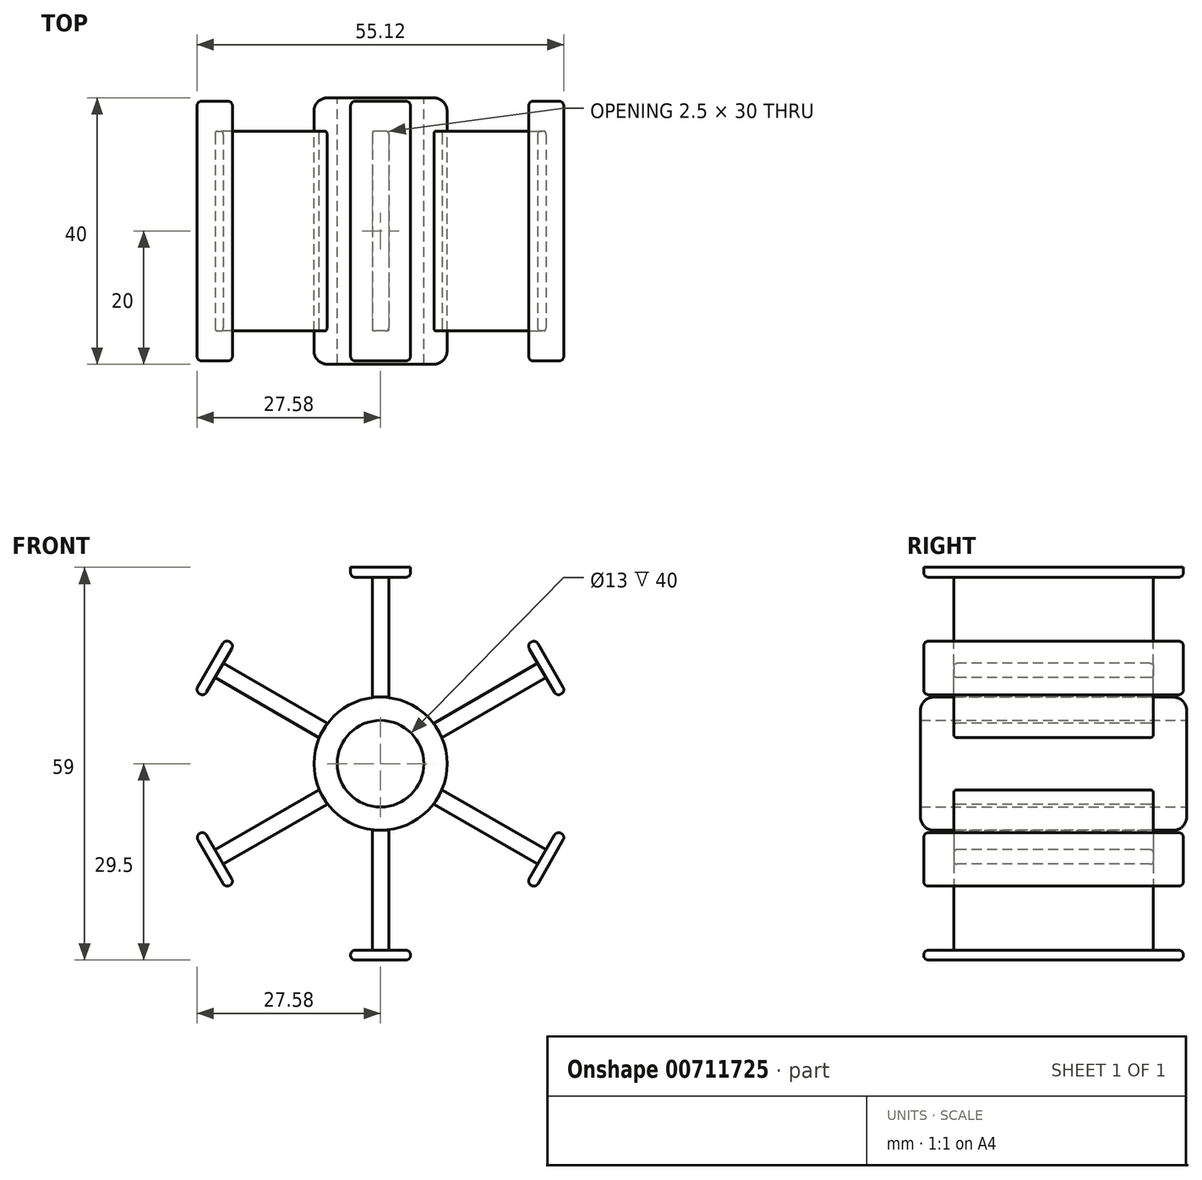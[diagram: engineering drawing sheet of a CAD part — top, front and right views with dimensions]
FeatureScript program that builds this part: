
annotation { "Feature Type Name" : "Feature", "Feature Type Description" : "" }
export const myFeature = defineFeature(function(context is Context, id is Id, definition is map)
    precondition{}
    {
        {
            var Q0;
            Q0=qCreatedBy(makeId("Front.planeOp"),FACE);
            var sketch = newSketch(context, id + "F0", { "sketchPlane" : qUnion([Q0])});
            skCircle(sketch, "E0", {"center": v(0, 0) * mm, "radius": 31 * mm});
            skCircle(sketch, "E1", {"center": v(0, 0) * mm, "radius": 6 * mm});
            skCircle(sketch, "E2", {"center": v(0, 0) * mm, "radius": 6.5 * mm});
            skCircle(sketch, "E3", {"center": v(0, 0) * mm, "radius": 10 * mm});
            skLineSegment(sketch, "E4", {"start": v(0, 10) * mm, "end": v(0, 28) * mm});
            skLineSegment(sketch, "E5.1.0", {"start": v(-8.66, -5) * mm, "end": v(-24.25, -14) * mm});
            skLineSegment(sketch, "E5.2.0", {"start": v(8.66, -5) * mm, "end": v(24.25, -14) * mm});
            skLineSegment(sketch, "E6", {"start": v(0, -10) * mm, "end": v(0, -28) * mm});
            skLineSegment(sketch, "E7.1.0", {"start": v(-8.66, 5) * mm, "end": v(-24.25, 14) * mm});
            skLineSegment(sketch, "E7.2.0", {"start": v(8.66, 5) * mm, "end": v(24.25, 14) * mm});
            skSolve(sketch);
        }
        {
            var Q0;
            Q0=makeQuery(id+"F0.imprint","IMPRINT",FACE,{"disambiguationData":[TD([[makeQuery(id+"F0.imprint","IMPRINT",EDGE,{"derivedFrom":sQuery(id+"F0.wireOp",EDGE,"E2")}),-1.0]])]});
            extrude(context, id + "F1", {"entities" : qUnion([Q0]), "endBound" : BoundingType.SYMMETRIC, "depth" : 40 * mm, "offsetDistance" : 25 * mm});
        }
        {
            var Q0;
            Q0=sQuery(id+"F0.wireOp",EDGE,"E4");
            var Q1;
            Q1=sQuery(id+"F0.wireOp",EDGE,"E5.2.0");
            var Q2;
            Q2=sQuery(id+"F0.wireOp",EDGE,"E5.1.0");
            var Q3;
            Q3=sQuery(id+"F0.wireOp",EDGE,"E7.1.0");
            var Q4;
            Q4=sQuery(id+"F0.wireOp",EDGE,"E7.2.0");
            var Q5;
            Q5=sQuery(id+"F0.wireOp",EDGE,"E6");
            extrude(context, id + "F2", {"bodyType" : ToolBodyType.SURFACE, "surfaceEntities" : qUnion([Q0, Q1, Q2, Q3, Q4, Q5]), "endBound" : BoundingType.SYMMETRIC, "depth" : 30 * mm, "offsetDistance" : 25 * mm});
        }
        {
            var Q0;
            Q0=makeQuery(id+"F2.opExtrude","SWEPT_FACE",FACE,{"disambiguationData":[OSD([sQuery(id+"F0.wireOp",EDGE,"E4")])]});
            extrude(context, id + "F3", {"entities" : qUnion([Q0]), "operationType" : NewBodyOperationType.ADD, "endBound" : BoundingType.SYMMETRIC, "depth" : 2.5 * mm, "offsetDistance" : 25 * mm});
        }
        {
            var Q0;
            Q0=makeQuery(id+"F2.opExtrude","SWEPT_FACE",FACE,{"disambiguationData":[OSD([sQuery(id+"F0.wireOp",EDGE,"E5.1.0")])]});
            extrude(context, id + "F4", {"entities" : qUnion([Q0]), "operationType" : NewBodyOperationType.ADD, "endBound" : BoundingType.SYMMETRIC, "depth" : 2.5 * mm, "offsetDistance" : 25 * mm});
        }
        {
            var Q0;
            Q0=makeQuery(id+"F2.opExtrude","SWEPT_FACE",FACE,{"disambiguationData":[OSD([sQuery(id+"F0.wireOp",EDGE,"E5.2.0")])]});
            extrude(context, id + "F5", {"entities" : qUnion([Q0]), "operationType" : NewBodyOperationType.ADD, "endBound" : BoundingType.SYMMETRIC, "depth" : 2.5 * mm, "offsetDistance" : 25 * mm});
        }
        {
            var Q0;
            {var subQ0=sQuery(id+"F0.wireOp",EDGE,"E5.1.0");Q0=makeQuery(id+"F4.opExtrude","CAP_EDGE",EDGE,{"disambiguationData":[OSD([subQ0]),TDD([makeQuery(id+"F2.opExtrude","CAP_EDGE",EDGE,{"disambiguationData":[OSD([subQ0])],"isStart":false})])],"isStart":false});}
            var Q1;
            {var subQ0=sQuery(id+"F0.wireOp",EDGE,"E5.1.0");Q1=makeQuery(id+"F4.opExtrude","CAP_EDGE",EDGE,{"disambiguationData":[OSD([subQ0]),TDD([makeQuery(id+"F2.opExtrude","CAP_EDGE",EDGE,{"disambiguationData":[OSD([subQ0])],"isStart":false})])],"isStart":true});}
            var Q2;
            {var subQ0=sQuery(id+"F0.wireOp",EDGE,"E5.1.0");Q2=makeQuery(id+"F4.opExtrude","CAP_EDGE",EDGE,{"disambiguationData":[OSD([subQ0]),TDD([makeQuery(id+"F2.opExtrude","CAP_EDGE",EDGE,{"disambiguationData":[OSD([subQ0])],"isStart":true})])],"isStart":true});}
            var Q3;
            {var subQ0=sQuery(id+"F0.wireOp",EDGE,"E5.1.0");Q3=makeQuery(id+"F4.opExtrude","CAP_EDGE",EDGE,{"disambiguationData":[OSD([subQ0]),TDD([makeQuery(id+"F2.opExtrude","CAP_EDGE",EDGE,{"disambiguationData":[OSD([subQ0])],"isStart":true})])],"isStart":false});}
            var Q4;
            {var subQ0=sQuery(id+"F0.wireOp",EDGE,"E4");Q4=makeQuery(id+"F3.opExtrude","CAP_EDGE",EDGE,{"disambiguationData":[OSD([subQ0]),TDD([makeQuery(id+"F2.opExtrude","CAP_EDGE",EDGE,{"disambiguationData":[OSD([subQ0])],"isStart":false})])],"isStart":true});}
            var Q5;
            {var subQ0=sQuery(id+"F0.wireOp",EDGE,"E4");Q5=makeQuery(id+"F3.opExtrude","CAP_EDGE",EDGE,{"disambiguationData":[OSD([subQ0]),TDD([makeQuery(id+"F2.opExtrude","CAP_EDGE",EDGE,{"disambiguationData":[OSD([subQ0])],"isStart":false})])],"isStart":false});}
            var Q6;
            {var subQ0=sQuery(id+"F0.wireOp",EDGE,"E4");Q6=makeQuery(id+"F3.opExtrude","CAP_EDGE",EDGE,{"disambiguationData":[OSD([subQ0]),TDD([makeQuery(id+"F2.opExtrude","CAP_EDGE",EDGE,{"disambiguationData":[OSD([subQ0])],"isStart":true})])],"isStart":false});}
            var Q7;
            {var subQ0=sQuery(id+"F0.wireOp",EDGE,"E4");Q7=makeQuery(id+"F3.opExtrude","CAP_EDGE",EDGE,{"disambiguationData":[OSD([subQ0]),TDD([makeQuery(id+"F2.opExtrude","CAP_EDGE",EDGE,{"disambiguationData":[OSD([subQ0])],"isStart":true})])],"isStart":true});}
            var Q8;
            {var subQ0=sQuery(id+"F0.wireOp",EDGE,"E5.2.0");Q8=makeQuery(id+"F5.opExtrude","CAP_EDGE",EDGE,{"disambiguationData":[OSD([subQ0]),TDD([makeQuery(id+"F2.opExtrude","CAP_EDGE",EDGE,{"disambiguationData":[OSD([subQ0])],"isStart":true})])],"isStart":true});}
            var Q9;
            {var subQ0=sQuery(id+"F0.wireOp",EDGE,"E5.2.0");Q9=makeQuery(id+"F5.opExtrude","CAP_EDGE",EDGE,{"disambiguationData":[OSD([subQ0]),TDD([makeQuery(id+"F2.opExtrude","CAP_EDGE",EDGE,{"disambiguationData":[OSD([subQ0])],"isStart":true})])],"isStart":false});}
            var Q10;
            {var subQ0=sQuery(id+"F0.wireOp",EDGE,"E5.2.0");Q10=makeQuery(id+"F5.opExtrude","CAP_EDGE",EDGE,{"disambiguationData":[OSD([subQ0]),TDD([makeQuery(id+"F2.opExtrude","CAP_EDGE",EDGE,{"disambiguationData":[OSD([subQ0])],"isStart":false})])],"isStart":true});}
            var Q11;
            {var subQ0=sQuery(id+"F0.wireOp",EDGE,"E5.2.0");Q11=makeQuery(id+"F5.opExtrude","CAP_EDGE",EDGE,{"disambiguationData":[OSD([subQ0]),TDD([makeQuery(id+"F2.opExtrude","CAP_EDGE",EDGE,{"disambiguationData":[OSD([subQ0])],"isStart":false})])],"isStart":false});}
            fillet(context, id + "F6", {"entities" : qUnion([Q0, Q1, Q2, Q3, Q4, Q5, Q6, Q7, Q8, Q9, Q10, Q11]), "radius" : 0.5 * mm, "tangentPropagation" : true, "allowEdgeOverflow" : false});
        }
        {
            var Q0;
            Q0=makeQuery(id+"F5.opExtrude","SWEPT_FACE",FACE,{"disambiguationData":[OSD([sQuery(id+"F0.wireOp",VERTEX,"E5.2.0.end")])]});
            var sketch = newSketch(context, id + "F7", { "sketchPlane" : qUnion([Q0])});
            skLineSegment(sketch, "E8.bottom", {"start": v(19.5, 4.5) * mm, "end": v(-19.5, 4.5) * mm});
            skLineSegment(sketch, "E8.top", {"start": v(19.5, -4.5) * mm, "end": v(-19.5, -4.5) * mm});
            skLineSegment(sketch, "E8.left", {"start": v(19.5, 4.5) * mm, "end": v(19.5, -4.5) * mm});
            skLineSegment(sketch, "E8.right", {"start": v(-19.5, 4.5) * mm, "end": v(-19.5, -4.5) * mm});
            skPoint(sketch, "E8.middle", {"position": v(0, 0) * mm});
            skSolve(sketch);
        }
        {
            var Q0;
            Q0 = qSketchRegion(id + "F7", true);
            extrude(context, id + "F8", {"entities" : qUnion([Q0]), "operationType" : NewBodyOperationType.ADD, "depth" : 1.5 * mm, "offsetDistance" : 25 * mm});
        }
        {
            var Q0;
            Q0=makeQuery(id+"F5.opExtrude","CAP_EDGE",EDGE,{"disambiguationData":[OSD([sQuery(id+"F0.wireOp",VERTEX,"E5.2.0.end")])],"isStart":true});
            var Q1;
            Q1=makeQuery(id+"F5.opExtrude","CAP_EDGE",EDGE,{"disambiguationData":[OSD([sQuery(id+"F0.wireOp",VERTEX,"E5.2.0.end")])],"isStart":false});
            var Q2;
            Q2=makeQuery(id+"F8.opExtrude","SWEPT_EDGE",EDGE,{"disambiguationData":[OSD([sQuery(id+"F7.wireOp",EDGE,"E8.top"),sQuery(id+"F7.wireOp",EDGE,"E8.right")])]});
            var Q3;
            Q3=makeQuery(id+"F8.opExtrude","SWEPT_EDGE",EDGE,{"disambiguationData":[OSD([sQuery(id+"F7.wireOp",EDGE,"E8.bottom"),sQuery(id+"F7.wireOp",EDGE,"E8.right")])]});
            var Q4;
            Q4=makeQuery(id+"F8.opExtrude","SWEPT_EDGE",EDGE,{"disambiguationData":[OSD([sQuery(id+"F7.wireOp",EDGE,"E8.top"),sQuery(id+"F7.wireOp",EDGE,"E8.left")])]});
            var Q5;
            Q5=makeQuery(id+"F8.opExtrude","SWEPT_EDGE",EDGE,{"disambiguationData":[OSD([sQuery(id+"F7.wireOp",EDGE,"E8.bottom"),sQuery(id+"F7.wireOp",EDGE,"E8.left")])]});
            var Q6;
            Q6=makeQuery(id+"F8.opExtrude","CAP_EDGE",EDGE,{"disambiguationData":[OSD([sQuery(id+"F7.wireOp",EDGE,"E8.right")])],"isStart":true});
            var Q7;
            Q7=makeQuery(id+"F8.opExtrude","CAP_EDGE",EDGE,{"disambiguationData":[OSD([sQuery(id+"F7.wireOp",EDGE,"E8.bottom")])],"isStart":true});
            var Q8;
            Q8=makeQuery(id+"F8.opExtrude","CAP_EDGE",EDGE,{"disambiguationData":[OSD([sQuery(id+"F7.wireOp",EDGE,"E8.left")])],"isStart":true});
            var Q9;
            Q9=makeQuery(id+"F8.opExtrude","CAP_EDGE",EDGE,{"disambiguationData":[OSD([sQuery(id+"F7.wireOp",EDGE,"E8.top")])],"isStart":true});
            var Q10;
            Q10=makeQuery(id+"F8.opExtrude","CAP_FACE",FACE,{"disambiguationData":[OSD([sQuery(id+"F7.wireOp",EDGE,"E8.bottom"),sQuery(id+"F7.wireOp",EDGE,"E8.top"),sQuery(id+"F7.wireOp",EDGE,"E8.left"),sQuery(id+"F7.wireOp",EDGE,"E8.right")])],"isStart":false});
            fillet(context, id + "F9", {"entities" : qUnion([Q0, Q1, Q2, Q3, Q4, Q5, Q6, Q7, Q8, Q9, Q10]), "radius" : .7 * mm, "tangentPropagation" : true, "allowEdgeOverflow" : false});
        }
        {
            var Q0;
            Q0=makeQuery(id+"F3.opExtrude","SWEPT_FACE",FACE,{"disambiguationData":[OSD([sQuery(id+"F0.wireOp",VERTEX,"E4.end")])]});
            var sketch = newSketch(context, id + "F10", { "sketchPlane" : qUnion([Q0])});
            skLineSegment(sketch, "E9.bottom", {"start": v(4.5, 19.5) * mm, "end": v(-4.5, 19.5) * mm});
            skLineSegment(sketch, "E9.top", {"start": v(4.5, -19.5) * mm, "end": v(-4.5, -19.5) * mm});
            skLineSegment(sketch, "E9.left", {"start": v(4.5, 19.5) * mm, "end": v(4.5, -19.5) * mm});
            skLineSegment(sketch, "E9.right", {"start": v(-4.5, 19.5) * mm, "end": v(-4.5, -19.5) * mm});
            skPoint(sketch, "E9.middle", {"position": v(0, 0) * mm});
            skSolve(sketch);
        }
        {
            var Q0;
            Q0=makeQuery(id+"F10.imprint","IMPRINT",FACE,{"disambiguationData":[TD([[makeQuery(id+"F10.imprint","IMPRINT",EDGE,{"derivedFrom":sQuery(id+"F10.wireOp",EDGE,"E9.bottom")}),1.0]])]});
            var Q1;
            {var subQ0=sQuery(id+"F0.wireOp",VERTEX,"E4.end");Q1=makeQuery(id+"F10.imprint","IMPRINT",FACE,{"disambiguationData":[TD([[makeQuery(id+"F10.imprint","IMPRINT",EDGE,{"derivedFrom":makeQuery(id+"F3.opExtrude","CAP_EDGE",EDGE,{"disambiguationData":[OSD([subQ0])],"isStart":true})}),1.0]])]});}
            extrude(context, id + "F11", {"entities" : qUnion([Q0, Q1]), "operationType" : NewBodyOperationType.ADD, "depth" : 1.5 * mm, "offsetDistance" : 25 * mm});
        }
        {
            var Q0;
            Q0=makeQuery(id+"F11.opExtrude","CAP_EDGE",EDGE,{"disambiguationData":[OSD([sQuery(id+"F10.wireOp",EDGE,"E9.left")])],"isStart":true});
            var Q1;
            Q1=makeQuery(id+"F11.opExtrude","CAP_EDGE",EDGE,{"disambiguationData":[OSD([sQuery(id+"F10.wireOp",EDGE,"E9.right")])],"isStart":true});
            var Q2;
            Q2=makeQuery(id+"F11.opExtrude","SWEPT_EDGE",EDGE,{"disambiguationData":[OSD([sQuery(id+"F10.wireOp",EDGE,"E9.bottom"),sQuery(id+"F10.wireOp",EDGE,"E9.right")])]});
            var Q3;
            Q3=makeQuery(id+"F11.opExtrude","SWEPT_EDGE",EDGE,{"disambiguationData":[OSD([sQuery(id+"F10.wireOp",EDGE,"E9.top"),sQuery(id+"F10.wireOp",EDGE,"E9.right")])]});
            var Q4;
            Q4=makeQuery(id+"F11.opExtrude","SWEPT_EDGE",EDGE,{"disambiguationData":[OSD([sQuery(id+"F10.wireOp",EDGE,"E9.top"),sQuery(id+"F10.wireOp",EDGE,"E9.left")])]});
            var Q5;
            Q5=makeQuery(id+"F11.opExtrude","SWEPT_EDGE",EDGE,{"disambiguationData":[OSD([sQuery(id+"F10.wireOp",EDGE,"E9.bottom"),sQuery(id+"F10.wireOp",EDGE,"E9.left")])]});
            var Q6;
            Q6=makeQuery(id+"F11.opExtrude","CAP_EDGE",EDGE,{"disambiguationData":[OSD([sQuery(id+"F10.wireOp",EDGE,"E9.top")])],"isStart":true});
            var Q7;
            Q7=makeQuery(id+"F11.opExtrude","CAP_EDGE",EDGE,{"disambiguationData":[OSD([sQuery(id+"F10.wireOp",EDGE,"E9.bottom")])],"isStart":true});
            var Q8;
            Q8=makeQuery(id+"F3.opExtrude","CAP_EDGE",EDGE,{"disambiguationData":[OSD([sQuery(id+"F0.wireOp",VERTEX,"E4.end")])],"isStart":false});
            var Q9;
            {var subQ0=sQuery(id+"F0.wireOp",VERTEX,"E4.end");Q9=makeQuery(id+"F3.opExtrude","SWEPT_EDGE",EDGE,{"disambiguationData":[OSD([subQ0]),TDD([makeQuery(id+"F2.opExtrude","CAP_VERTEX",VERTEX,{"disambiguationData":[OSD([subQ0])],"isStart":false})])]});}
            var Q10;
            Q10=makeQuery(id+"F3.opExtrude","CAP_EDGE",EDGE,{"disambiguationData":[OSD([sQuery(id+"F0.wireOp",VERTEX,"E4.end")])],"isStart":true});
            var Q11;
            {var subQ0=sQuery(id+"F0.wireOp",VERTEX,"E4.end");Q11=makeQuery(id+"F3.opExtrude","SWEPT_EDGE",EDGE,{"disambiguationData":[OSD([subQ0]),TDD([makeQuery(id+"F2.opExtrude","CAP_VERTEX",VERTEX,{"disambiguationData":[OSD([subQ0])],"isStart":true})])]});}
            fillet(context, id + "F12", {"entities" : qUnion([Q0, Q1, Q2, Q3, Q4, Q5, Q6, Q7, Q8, Q9, Q10, Q11]), "radius" : .7 * mm, "tangentPropagation" : true, "allowEdgeOverflow" : false});
        }
        {
            var Q0;
            Q0=makeQuery(id+"F4.opExtrude","SWEPT_FACE",FACE,{"disambiguationData":[OSD([sQuery(id+"F0.wireOp",VERTEX,"E5.1.0.end")])]});
            var sketch = newSketch(context, id + "F13", { "sketchPlane" : qUnion([Q0])});
            skLineSegment(sketch, "E10.bottom", {"start": v(-19.5, 4.5) * mm, "end": v(19.5, 4.5) * mm});
            skLineSegment(sketch, "E10.top", {"start": v(-19.5, -4.5) * mm, "end": v(19.5, -4.5) * mm});
            skLineSegment(sketch, "E10.left", {"start": v(-19.5, 4.5) * mm, "end": v(-19.5, -4.5) * mm});
            skLineSegment(sketch, "E10.right", {"start": v(19.5, 4.5) * mm, "end": v(19.5, -4.5) * mm});
            skPoint(sketch, "E10.middle", {"position": v(0, 0) * mm});
            skSolve(sketch);
        }
        {
            var Q0;
            {var subQ0=sQuery(id+"F0.wireOp",VERTEX,"E5.1.0.end");Q0=makeQuery(id+"F13.imprint","IMPRINT",FACE,{"disambiguationData":[TD([[makeQuery(id+"F13.imprint","IMPRINT",EDGE,{"derivedFrom":makeQuery(id+"F4.opExtrude","CAP_EDGE",EDGE,{"disambiguationData":[OSD([subQ0])],"isStart":true})}),1.0]])]});}
            var Q1;
            Q1=makeQuery(id+"F13.imprint","IMPRINT",FACE,{"disambiguationData":[TD([[makeQuery(id+"F13.imprint","IMPRINT",EDGE,{"derivedFrom":sQuery(id+"F13.wireOp",EDGE,"E10.bottom")}),-1.0]])]});
            extrude(context, id + "F14", {"entities" : qUnion([Q0, Q1]), "operationType" : NewBodyOperationType.ADD, "depth" : 1.5 * mm, "offsetDistance" : 25 * mm});
        }
        {
            var Q0;
            Q0=makeQuery(id+"F14.opExtrude","SWEPT_EDGE",EDGE,{"disambiguationData":[OSD([sQuery(id+"F13.wireOp",EDGE,"E10.top"),sQuery(id+"F13.wireOp",EDGE,"E10.left")])]});
            var Q1;
            Q1=makeQuery(id+"F14.opExtrude","SWEPT_EDGE",EDGE,{"disambiguationData":[OSD([sQuery(id+"F13.wireOp",EDGE,"E10.bottom"),sQuery(id+"F13.wireOp",EDGE,"E10.left")])]});
            var Q2;
            Q2=makeQuery(id+"F14.opExtrude","SWEPT_EDGE",EDGE,{"disambiguationData":[OSD([sQuery(id+"F13.wireOp",EDGE,"E10.bottom"),sQuery(id+"F13.wireOp",EDGE,"E10.right")])]});
            var Q3;
            Q3=makeQuery(id+"F14.opExtrude","SWEPT_EDGE",EDGE,{"disambiguationData":[OSD([sQuery(id+"F13.wireOp",EDGE,"E10.top"),sQuery(id+"F13.wireOp",EDGE,"E10.right")])]});
            var Q4;
            Q4=makeQuery(id+"F14.opExtrude","CAP_EDGE",EDGE,{"disambiguationData":[OSD([sQuery(id+"F13.wireOp",EDGE,"E10.bottom")])],"isStart":true});
            var Q5;
            Q5=makeQuery(id+"F14.opExtrude","CAP_EDGE",EDGE,{"disambiguationData":[OSD([sQuery(id+"F13.wireOp",EDGE,"E10.right")])],"isStart":true});
            var Q6;
            Q6=makeQuery(id+"F14.opExtrude","CAP_EDGE",EDGE,{"disambiguationData":[OSD([sQuery(id+"F13.wireOp",EDGE,"E10.top")])],"isStart":true});
            var Q7;
            Q7=makeQuery(id+"F14.opExtrude","CAP_EDGE",EDGE,{"disambiguationData":[OSD([sQuery(id+"F13.wireOp",EDGE,"E10.left")])],"isStart":true});
            var Q8;
            Q8=makeQuery(id+"F4.opExtrude","CAP_EDGE",EDGE,{"disambiguationData":[OSD([sQuery(id+"F0.wireOp",VERTEX,"E5.1.0.end")])],"isStart":true});
            var Q9;
            Q9=makeQuery(id+"F4.opExtrude","CAP_EDGE",EDGE,{"disambiguationData":[OSD([sQuery(id+"F0.wireOp",VERTEX,"E5.1.0.end")])],"isStart":false});
            var Q10;
            {var subQ0=sQuery(id+"F0.wireOp",VERTEX,"E5.1.0.end");Q10=makeQuery(id+"F4.opExtrude","SWEPT_EDGE",EDGE,{"disambiguationData":[OSD([subQ0]),TDD([makeQuery(id+"F2.opExtrude","CAP_VERTEX",VERTEX,{"disambiguationData":[OSD([subQ0])],"isStart":true})])]});}
            var Q11;
            {var subQ0=sQuery(id+"F0.wireOp",VERTEX,"E5.1.0.end");Q11=makeQuery(id+"F4.opExtrude","SWEPT_EDGE",EDGE,{"disambiguationData":[OSD([subQ0]),TDD([makeQuery(id+"F2.opExtrude","CAP_VERTEX",VERTEX,{"disambiguationData":[OSD([subQ0])],"isStart":false})])]});}
            var Q12;
            Q12=makeQuery(id+"F14.opExtrude","CAP_FACE",FACE,{"disambiguationData":[OSD([sQuery(id+"F13.wireOp",EDGE,"E10.bottom"),sQuery(id+"F13.wireOp",EDGE,"E10.top"),sQuery(id+"F13.wireOp",EDGE,"E10.left"),sQuery(id+"F13.wireOp",EDGE,"E10.right")])],"isStart":false});
            fillet(context, id + "F15", {"entities" : qUnion([Q0, Q1, Q2, Q3, Q4, Q5, Q6, Q7, Q8, Q9, Q10, Q11, Q12]), "radius" : .7 * mm, "tangentPropagation" : true, "allowEdgeOverflow" : false});
        }
        {
            var Q0;
            Q0=makeQuery(id+"F1.opExtrude","CAP_EDGE",EDGE,{"disambiguationData":[OSD([sQuery(id+"F0.wireOp",EDGE,"E3")])],"isStart":true});
            var Q1;
            Q1=makeQuery(id+"F1.opExtrude","CAP_EDGE",EDGE,{"disambiguationData":[OSD([sQuery(id+"F0.wireOp",EDGE,"E3")])],"isStart":false});
            fillet(context, id + "F16", {"entities" : qUnion([Q0, Q1]), "radius" : 2 * mm, "tangentPropagation" : true, "allowEdgeOverflow" : false});
        }
        {
            var Q0;
            Q0=makeQuery(id+"F2.opExtrude","SWEPT_FACE",FACE,{"disambiguationData":[OSD([sQuery(id+"F0.wireOp",EDGE,"E7.2.0")])]});
            extrude(context, id + "F17", {"entities" : qUnion([Q0]), "operationType" : NewBodyOperationType.ADD, "endBound" : BoundingType.SYMMETRIC, "depth" : 2.5 * mm, "offsetDistance" : 25 * mm});
        }
        {
            var Q0;
            Q0=makeQuery(id+"F2.opExtrude","SWEPT_FACE",FACE,{"disambiguationData":[OSD([sQuery(id+"F0.wireOp",EDGE,"E7.1.0")])]});
            extrude(context, id + "F18", {"entities" : qUnion([Q0]), "operationType" : NewBodyOperationType.ADD, "endBound" : BoundingType.SYMMETRIC, "depth" : 2.5 * mm, "offsetDistance" : 25 * mm});
        }
        {
            var Q0;
            Q0=makeQuery(id+"F2.opExtrude","SWEPT_FACE",FACE,{"disambiguationData":[OSD([sQuery(id+"F0.wireOp",EDGE,"E6")])]});
            extrude(context, id + "F19", {"entities" : qUnion([Q0]), "operationType" : NewBodyOperationType.ADD, "endBound" : BoundingType.SYMMETRIC, "depth" : 2.5 * mm, "offsetDistance" : 25 * mm});
        }
        {
            var Q0;
            Q0=makeQuery(id+"F19.opExtrude","SWEPT_FACE",FACE,{"disambiguationData":[OSD([sQuery(id+"F0.wireOp",VERTEX,"E6.end")])]});
            var sketch = newSketch(context, id + "F20", { "sketchPlane" : qUnion([Q0])});
            skLineSegment(sketch, "E11.bottom", {"start": v(4.5, 19.5) * mm, "end": v(-4.5, 19.5) * mm});
            skLineSegment(sketch, "E11.top", {"start": v(4.5, -19.5) * mm, "end": v(-4.5, -19.5) * mm});
            skLineSegment(sketch, "E11.left", {"start": v(4.5, 19.5) * mm, "end": v(4.5, -19.5) * mm});
            skLineSegment(sketch, "E11.right", {"start": v(-4.5, 19.5) * mm, "end": v(-4.5, -19.5) * mm});
            skPoint(sketch, "E11.middle", {"position": v(0, 0) * mm});
            skSolve(sketch);
        }
        {
            var Q0;
            Q0=makeQuery(id+"F17.opExtrude","SWEPT_FACE",FACE,{"disambiguationData":[OSD([sQuery(id+"F0.wireOp",VERTEX,"E7.2.0.end")])]});
            var sketch = newSketch(context, id + "F21", { "sketchPlane" : qUnion([Q0])});
            skLineSegment(sketch, "E12.bottom", {"start": v(19.5, 4.5) * mm, "end": v(-19.5, 4.5) * mm});
            skLineSegment(sketch, "E12.top", {"start": v(19.5, -4.5) * mm, "end": v(-19.5, -4.5) * mm});
            skLineSegment(sketch, "E12.left", {"start": v(19.5, 4.5) * mm, "end": v(19.5, -4.5) * mm});
            skLineSegment(sketch, "E12.right", {"start": v(-19.5, 4.5) * mm, "end": v(-19.5, -4.5) * mm});
            skPoint(sketch, "E12.middle", {"position": v(0, 0) * mm});
            skSolve(sketch);
        }
        {
            var Q0;
            Q0=makeQuery(id+"F18.opExtrude","SWEPT_FACE",FACE,{"disambiguationData":[OSD([sQuery(id+"F0.wireOp",VERTEX,"E7.1.0.end")])]});
            var sketch = newSketch(context, id + "F22", { "sketchPlane" : qUnion([Q0])});
            skLineSegment(sketch, "E13.bottom", {"start": v(-19.5, 4.5) * mm, "end": v(19.5, 4.5) * mm});
            skLineSegment(sketch, "E13.top", {"start": v(-19.5, -4.5) * mm, "end": v(19.5, -4.5) * mm});
            skLineSegment(sketch, "E13.left", {"start": v(-19.5, 4.5) * mm, "end": v(-19.5, -4.5) * mm});
            skLineSegment(sketch, "E13.right", {"start": v(19.5, 4.5) * mm, "end": v(19.5, -4.5) * mm});
            skPoint(sketch, "E13.middle", {"position": v(0, 0) * mm});
            skSolve(sketch);
        }
        {
            var Q0;
            Q0 = qSketchRegion(id + "F20", true);
            extrude(context, id + "F23", {"entities" : qUnion([Q0]), "operationType" : NewBodyOperationType.ADD, "depth" : 1.5 * mm, "offsetDistance" : 25 * mm});
        }
        {
            var Q0;
            Q0 = qSketchRegion(id + "F21", true);
            extrude(context, id + "F24", {"entities" : qUnion([Q0]), "operationType" : NewBodyOperationType.ADD, "depth" : 1.5 * mm, "offsetDistance" : 25 * mm});
        }
        {
            var Q0;
            Q0 = qSketchRegion(id + "F22", true);
            extrude(context, id + "F25", {"entities" : qUnion([Q0]), "operationType" : NewBodyOperationType.ADD, "depth" : 1.55 * mm, "offsetDistance" : 25 * mm});
        }
        {
            var Q0;
            {var subQ0=sQuery(id+"F0.wireOp",EDGE,"E7.2.0");Q0=makeQuery(id+"F17.opExtrude","CAP_EDGE",EDGE,{"disambiguationData":[OSD([subQ0]),TDD([makeQuery(id+"F2.opExtrude","CAP_EDGE",EDGE,{"disambiguationData":[OSD([subQ0])],"isStart":false})])],"isStart":false});}
            var Q1;
            {var subQ0=sQuery(id+"F0.wireOp",EDGE,"E7.2.0");Q1=makeQuery(id+"F17.opExtrude","CAP_EDGE",EDGE,{"disambiguationData":[OSD([subQ0]),TDD([makeQuery(id+"F2.opExtrude","CAP_EDGE",EDGE,{"disambiguationData":[OSD([subQ0])],"isStart":false})])],"isStart":true});}
            var Q2;
            {var subQ0=sQuery(id+"F0.wireOp",EDGE,"E7.2.0");Q2=makeQuery(id+"F17.opExtrude","CAP_EDGE",EDGE,{"disambiguationData":[OSD([subQ0]),TDD([makeQuery(id+"F2.opExtrude","CAP_EDGE",EDGE,{"disambiguationData":[OSD([subQ0])],"isStart":true})])],"isStart":false});}
            var Q3;
            {var subQ0=sQuery(id+"F0.wireOp",EDGE,"E7.2.0");Q3=makeQuery(id+"F17.opExtrude","CAP_EDGE",EDGE,{"disambiguationData":[OSD([subQ0]),TDD([makeQuery(id+"F2.opExtrude","CAP_EDGE",EDGE,{"disambiguationData":[OSD([subQ0])],"isStart":true})])],"isStart":true});}
            var Q4;
            {var subQ0=sQuery(id+"F0.wireOp",EDGE,"E6");Q4=makeQuery(id+"F19.opExtrude","CAP_EDGE",EDGE,{"disambiguationData":[OSD([subQ0]),TDD([makeQuery(id+"F2.opExtrude","CAP_EDGE",EDGE,{"disambiguationData":[OSD([subQ0])],"isStart":true})])],"isStart":true});}
            var Q5;
            {var subQ0=sQuery(id+"F0.wireOp",EDGE,"E6");Q5=makeQuery(id+"F19.opExtrude","CAP_EDGE",EDGE,{"disambiguationData":[OSD([subQ0]),TDD([makeQuery(id+"F2.opExtrude","CAP_EDGE",EDGE,{"disambiguationData":[OSD([subQ0])],"isStart":false})])],"isStart":true});}
            var Q6;
            {var subQ0=sQuery(id+"F0.wireOp",EDGE,"E6");Q6=makeQuery(id+"F19.opExtrude","CAP_EDGE",EDGE,{"disambiguationData":[OSD([subQ0]),TDD([makeQuery(id+"F2.opExtrude","CAP_EDGE",EDGE,{"disambiguationData":[OSD([subQ0])],"isStart":false})])],"isStart":false});}
            var Q7;
            {var subQ0=sQuery(id+"F0.wireOp",EDGE,"E6");Q7=makeQuery(id+"F19.opExtrude","CAP_EDGE",EDGE,{"disambiguationData":[OSD([subQ0]),TDD([makeQuery(id+"F2.opExtrude","CAP_EDGE",EDGE,{"disambiguationData":[OSD([subQ0])],"isStart":true})])],"isStart":false});}
            var Q8;
            {var subQ0=sQuery(id+"F0.wireOp",EDGE,"E7.1.0");Q8=makeQuery(id+"F18.opExtrude","CAP_EDGE",EDGE,{"disambiguationData":[OSD([subQ0]),TDD([makeQuery(id+"F2.opExtrude","CAP_EDGE",EDGE,{"disambiguationData":[OSD([subQ0])],"isStart":false})])],"isStart":true});}
            var Q9;
            {var subQ0=sQuery(id+"F0.wireOp",EDGE,"E7.1.0");Q9=makeQuery(id+"F18.opExtrude","CAP_EDGE",EDGE,{"disambiguationData":[OSD([subQ0]),TDD([makeQuery(id+"F2.opExtrude","CAP_EDGE",EDGE,{"disambiguationData":[OSD([subQ0])],"isStart":false})])],"isStart":false});}
            var Q10;
            {var subQ0=sQuery(id+"F0.wireOp",EDGE,"E7.1.0");Q10=makeQuery(id+"F18.opExtrude","CAP_EDGE",EDGE,{"disambiguationData":[OSD([subQ0]),TDD([makeQuery(id+"F2.opExtrude","CAP_EDGE",EDGE,{"disambiguationData":[OSD([subQ0])],"isStart":true})])],"isStart":false});}
            var Q11;
            {var subQ0=sQuery(id+"F0.wireOp",EDGE,"E7.1.0");Q11=makeQuery(id+"F18.opExtrude","CAP_EDGE",EDGE,{"disambiguationData":[OSD([subQ0]),TDD([makeQuery(id+"F2.opExtrude","CAP_EDGE",EDGE,{"disambiguationData":[OSD([subQ0])],"isStart":true})])],"isStart":true});}
            fillet(context, id + "F26", {"entities" : qUnion([Q0, Q1, Q2, Q3, Q4, Q5, Q6, Q7, Q8, Q9, Q10, Q11]), "radius" : 0.5 * mm, "tangentPropagation" : true, "allowEdgeOverflow" : false});
        }
        {
            var Q0;
            Q0=makeQuery(id+"F23.opExtrude","CAP_EDGE",EDGE,{"disambiguationData":[OSD([sQuery(id+"F20.wireOp",EDGE,"E11.right")])],"isStart":true});
            var Q1;
            Q1=makeQuery(id+"F19.opExtrude","CAP_EDGE",EDGE,{"disambiguationData":[OSD([sQuery(id+"F0.wireOp",VERTEX,"E6.end")])],"isStart":false});
            var Q2;
            Q2=makeQuery(id+"F19.opExtrude","CAP_EDGE",EDGE,{"disambiguationData":[OSD([sQuery(id+"F0.wireOp",VERTEX,"E6.end")])],"isStart":true});
            var Q3;
            {var subQ0=sQuery(id+"F0.wireOp",VERTEX,"E6.end");Q3=makeQuery(id+"F19.opExtrude","SWEPT_EDGE",EDGE,{"disambiguationData":[OSD([subQ0]),TDD([makeQuery(id+"F2.opExtrude","CAP_VERTEX",VERTEX,{"disambiguationData":[OSD([subQ0])],"isStart":true})])]});}
            var Q4;
            {var subQ0=sQuery(id+"F0.wireOp",VERTEX,"E6.end");Q4=makeQuery(id+"F19.opExtrude","SWEPT_EDGE",EDGE,{"disambiguationData":[OSD([subQ0]),TDD([makeQuery(id+"F2.opExtrude","CAP_VERTEX",VERTEX,{"disambiguationData":[OSD([subQ0])],"isStart":false})])]});}
            var Q5;
            Q5=makeQuery(id+"F23.opExtrude","CAP_EDGE",EDGE,{"disambiguationData":[OSD([sQuery(id+"F20.wireOp",EDGE,"E11.bottom")])],"isStart":true});
            var Q6;
            Q6=makeQuery(id+"F23.opExtrude","CAP_EDGE",EDGE,{"disambiguationData":[OSD([sQuery(id+"F20.wireOp",EDGE,"E11.left")])],"isStart":true});
            var Q7;
            Q7=makeQuery(id+"F23.opExtrude","SWEPT_EDGE",EDGE,{"disambiguationData":[OSD([sQuery(id+"F20.wireOp",EDGE,"E11.bottom"),sQuery(id+"F20.wireOp",EDGE,"E11.left")])]});
            var Q8;
            Q8=makeQuery(id+"F23.opExtrude","SWEPT_EDGE",EDGE,{"disambiguationData":[OSD([sQuery(id+"F20.wireOp",EDGE,"E11.bottom"),sQuery(id+"F20.wireOp",EDGE,"E11.right")])]});
            var Q9;
            Q9=makeQuery(id+"F23.opExtrude","SWEPT_EDGE",EDGE,{"disambiguationData":[OSD([sQuery(id+"F20.wireOp",EDGE,"E11.top"),sQuery(id+"F20.wireOp",EDGE,"E11.left")])]});
            var Q10;
            Q10=makeQuery(id+"F23.opExtrude","SWEPT_EDGE",EDGE,{"disambiguationData":[OSD([sQuery(id+"F20.wireOp",EDGE,"E11.top"),sQuery(id+"F20.wireOp",EDGE,"E11.right")])]});
            var Q11;
            Q11=makeQuery(id+"F23.opExtrude","CAP_EDGE",EDGE,{"disambiguationData":[OSD([sQuery(id+"F20.wireOp",EDGE,"E11.top")])],"isStart":true});
            var Q12;
            Q12=makeQuery(id+"F23.opExtrude","CAP_FACE",FACE,{"disambiguationData":[OSD([sQuery(id+"F20.wireOp",EDGE,"E11.bottom"),sQuery(id+"F20.wireOp",EDGE,"E11.top"),sQuery(id+"F20.wireOp",EDGE,"E11.left"),sQuery(id+"F20.wireOp",EDGE,"E11.right")])],"isStart":false});
            fillet(context, id + "F27", {"entities" : qUnion([Q0, Q1, Q2, Q3, Q4, Q5, Q6, Q7, Q8, Q9, Q10, Q11, Q12]), "radius" : .7 * mm, "tangentPropagation" : true, "allowEdgeOverflow" : false});
        }
        {
            var Q0;
            Q0=makeQuery(id+"F17.opExtrude","CAP_EDGE",EDGE,{"disambiguationData":[OSD([sQuery(id+"F0.wireOp",VERTEX,"E7.2.0.end")])],"isStart":false});
            var Q1;
            Q1=makeQuery(id+"F24.opExtrude","CAP_EDGE",EDGE,{"disambiguationData":[OSD([sQuery(id+"F21.wireOp",EDGE,"E12.top")])],"isStart":true});
            var Q2;
            Q2=makeQuery(id+"F24.opExtrude","CAP_EDGE",EDGE,{"disambiguationData":[OSD([sQuery(id+"F21.wireOp",EDGE,"E12.left")])],"isStart":true});
            var Q3;
            Q3=makeQuery(id+"F24.opExtrude","CAP_EDGE",EDGE,{"disambiguationData":[OSD([sQuery(id+"F21.wireOp",EDGE,"E12.bottom")])],"isStart":true});
            var Q4;
            Q4=makeQuery(id+"F24.opExtrude","SWEPT_EDGE",EDGE,{"disambiguationData":[OSD([sQuery(id+"F21.wireOp",EDGE,"E12.bottom"),sQuery(id+"F21.wireOp",EDGE,"E12.left")])]});
            var Q5;
            Q5=makeQuery(id+"F24.opExtrude","SWEPT_EDGE",EDGE,{"disambiguationData":[OSD([sQuery(id+"F21.wireOp",EDGE,"E12.top"),sQuery(id+"F21.wireOp",EDGE,"E12.left")])]});
            var Q6;
            Q6=makeQuery(id+"F24.opExtrude","SWEPT_EDGE",EDGE,{"disambiguationData":[OSD([sQuery(id+"F21.wireOp",EDGE,"E12.bottom"),sQuery(id+"F21.wireOp",EDGE,"E12.right")])]});
            var Q7;
            Q7=makeQuery(id+"F24.opExtrude","SWEPT_EDGE",EDGE,{"disambiguationData":[OSD([sQuery(id+"F21.wireOp",EDGE,"E12.top"),sQuery(id+"F21.wireOp",EDGE,"E12.right")])]});
            var Q8;
            Q8=makeQuery(id+"F24.opExtrude","CAP_EDGE",EDGE,{"disambiguationData":[OSD([sQuery(id+"F21.wireOp",EDGE,"E12.right")])],"isStart":true});
            var Q9;
            Q9=makeQuery(id+"F17.opExtrude","CAP_EDGE",EDGE,{"disambiguationData":[OSD([sQuery(id+"F0.wireOp",VERTEX,"E7.2.0.end")])],"isStart":true});
            var Q10;
            {var subQ0=sQuery(id+"F0.wireOp",VERTEX,"E7.2.0.end");Q10=makeQuery(id+"F17.opExtrude","SWEPT_EDGE",EDGE,{"disambiguationData":[OSD([subQ0]),TDD([makeQuery(id+"F2.opExtrude","CAP_VERTEX",VERTEX,{"disambiguationData":[OSD([subQ0])],"isStart":false})])]});}
            var Q11;
            {var subQ0=sQuery(id+"F0.wireOp",VERTEX,"E7.2.0.end");Q11=makeQuery(id+"F17.opExtrude","SWEPT_EDGE",EDGE,{"disambiguationData":[OSD([subQ0]),TDD([makeQuery(id+"F2.opExtrude","CAP_VERTEX",VERTEX,{"disambiguationData":[OSD([subQ0])],"isStart":true})])]});}
            var Q12;
            Q12=makeQuery(id+"F24.opExtrude","CAP_FACE",FACE,{"disambiguationData":[OSD([sQuery(id+"F21.wireOp",EDGE,"E12.bottom"),sQuery(id+"F21.wireOp",EDGE,"E12.top"),sQuery(id+"F21.wireOp",EDGE,"E12.left"),sQuery(id+"F21.wireOp",EDGE,"E12.right")])],"isStart":false});
            fillet(context, id + "F28", {"entities" : qUnion([Q0, Q1, Q2, Q3, Q4, Q5, Q6, Q7, Q8, Q9, Q10, Q11, Q12]), "radius" : .7 * mm, "tangentPropagation" : true, "allowEdgeOverflow" : false});
        }
        {
            var Q0;
            Q0=makeQuery(id+"F25.opExtrude","CAP_EDGE",EDGE,{"disambiguationData":[OSD([sQuery(id+"F22.wireOp",EDGE,"E13.bottom")])],"isStart":true});
            var Q1;
            Q1=makeQuery(id+"F25.opExtrude","SWEPT_EDGE",EDGE,{"disambiguationData":[OSD([sQuery(id+"F22.wireOp",EDGE,"E13.bottom"),sQuery(id+"F22.wireOp",EDGE,"E13.left")])]});
            var Q2;
            Q2=makeQuery(id+"F25.opExtrude","CAP_EDGE",EDGE,{"disambiguationData":[OSD([sQuery(id+"F22.wireOp",EDGE,"E13.left")])],"isStart":true});
            var Q3;
            Q3=makeQuery(id+"F25.opExtrude","SWEPT_EDGE",EDGE,{"disambiguationData":[OSD([sQuery(id+"F22.wireOp",EDGE,"E13.top"),sQuery(id+"F22.wireOp",EDGE,"E13.left")])]});
            var Q4;
            Q4=makeQuery(id+"F25.opExtrude","CAP_EDGE",EDGE,{"disambiguationData":[OSD([sQuery(id+"F22.wireOp",EDGE,"E13.top")])],"isStart":true});
            var Q5;
            Q5=makeQuery(id+"F25.opExtrude","SWEPT_EDGE",EDGE,{"disambiguationData":[OSD([sQuery(id+"F22.wireOp",EDGE,"E13.top"),sQuery(id+"F22.wireOp",EDGE,"E13.right")])]});
            var Q6;
            Q6=makeQuery(id+"F25.opExtrude","SWEPT_EDGE",EDGE,{"disambiguationData":[OSD([sQuery(id+"F22.wireOp",EDGE,"E13.bottom"),sQuery(id+"F22.wireOp",EDGE,"E13.right")])]});
            var Q7;
            Q7=makeQuery(id+"F25.opExtrude","CAP_EDGE",EDGE,{"disambiguationData":[OSD([sQuery(id+"F22.wireOp",EDGE,"E13.right")])],"isStart":true});
            var Q8;
            Q8=makeQuery(id+"F18.opExtrude","CAP_EDGE",EDGE,{"disambiguationData":[OSD([sQuery(id+"F0.wireOp",VERTEX,"E7.1.0.end")])],"isStart":true});
            var Q9;
            {var subQ0=sQuery(id+"F0.wireOp",VERTEX,"E7.1.0.end");Q9=makeQuery(id+"F18.opExtrude","SWEPT_EDGE",EDGE,{"disambiguationData":[OSD([subQ0]),TDD([makeQuery(id+"F2.opExtrude","CAP_VERTEX",VERTEX,{"disambiguationData":[OSD([subQ0])],"isStart":false})])]});}
            var Q10;
            Q10=makeQuery(id+"F18.opExtrude","CAP_EDGE",EDGE,{"disambiguationData":[OSD([sQuery(id+"F0.wireOp",VERTEX,"E7.1.0.end")])],"isStart":false});
            var Q11;
            {var subQ0=sQuery(id+"F0.wireOp",VERTEX,"E7.1.0.end");Q11=makeQuery(id+"F18.opExtrude","SWEPT_EDGE",EDGE,{"disambiguationData":[OSD([subQ0]),TDD([makeQuery(id+"F2.opExtrude","CAP_VERTEX",VERTEX,{"disambiguationData":[OSD([subQ0])],"isStart":true})])]});}
            var Q12;
            Q12=makeQuery(id+"F25.opExtrude","CAP_EDGE",EDGE,{"disambiguationData":[OSD([sQuery(id+"F22.wireOp",EDGE,"E13.bottom")])],"isStart":false});
            var Q13;
            Q13=makeQuery(id+"F25.opExtrude","CAP_EDGE",EDGE,{"disambiguationData":[OSD([sQuery(id+"F22.wireOp",EDGE,"E13.right")])],"isStart":false});
            var Q14;
            Q14=makeQuery(id+"F25.opExtrude","CAP_EDGE",EDGE,{"disambiguationData":[OSD([sQuery(id+"F22.wireOp",EDGE,"E13.top")])],"isStart":false});
            var Q15;
            Q15=makeQuery(id+"F25.opExtrude","CAP_EDGE",EDGE,{"disambiguationData":[OSD([sQuery(id+"F22.wireOp",EDGE,"E13.left")])],"isStart":false});
            fillet(context, id + "F29", {"entities" : qUnion([Q0, Q1, Q2, Q3, Q4, Q5, Q6, Q7, Q8, Q9, Q10, Q11, Q12, Q13, Q14, Q15]), "radius" : .7 * mm, "tangentPropagation" : true, "allowEdgeOverflow" : false});
        }
    });
